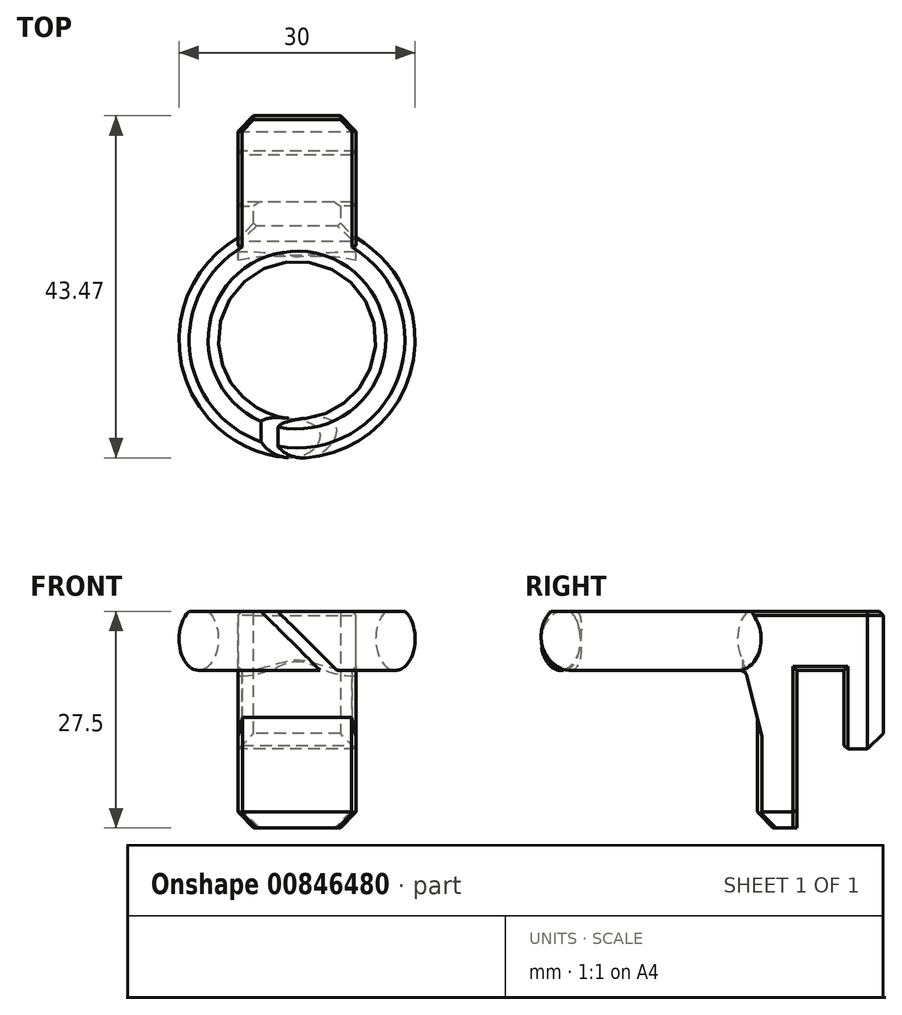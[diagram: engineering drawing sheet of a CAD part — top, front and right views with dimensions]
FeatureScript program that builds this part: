
annotation { "Feature Type Name" : "Feature", "Feature Type Description" : "" }
export const myFeature = defineFeature(function(context is Context, id is Id, definition is map)
    precondition{}
    {
        {
            var Q0;
            Q0=qCreatedBy(makeId("Front.planeOp"),FACE);
            var sketch = newSketch(context, id + "F0", { "sketchPlane" : qUnion([Q0])});
            skLineSegment(sketch, "E0", {"start": v(0, 10.58) * mm, "end": v(0, -9.7) * mm, "construction": true});
            skLineSegment(sketch, "E1", {"start": v(0, 0) * mm, "end": v(12.5, 0) * mm, "construction": true});
            skEllipse(sketch, "E2", {"center": v(12.5, 0) * mm, "majorRadius": 4 * mm, "minorRadius": 2.5 * mm, "majorAxis": v(0, 1)});
            skSolve(sketch);
        }
        {
            var Q0;
            Q0=qSketchRegion(id+"F0",true);
            var Q1;
            Q1=sQuery(id+"F0.wireOp",EDGE,"E0");
            revolve(context, id + "F1", {"surfaceOperationType" : NewSurfaceOperationType.NEW, "entities" : qUnion([Q0]), "axis" : qUnion([Q1]), "revolveType" : RevolveType.FULL});
        }
        {
            var Q0;
            Q0=qCreatedBy(makeId("Right.planeOp"),FACE);
            var sketch = newSketch(context, id + "F2", { "sketchPlane" : qUnion([Q0])});
            skLineSegment(sketch, "E3", {"start": v(12.5, 5) * mm, "end": v(28.5, 5) * mm});
            skLineSegment(sketch, "E4", {"start": v(28.5, 5) * mm, "end": v(28.5, -14) * mm});
            skLineSegment(sketch, "E5", {"start": v(28.5, -14) * mm, "end": v(23.5, -14) * mm});
            skLineSegment(sketch, "E6", {"start": v(23.5, -14) * mm, "end": v(23.5, -4) * mm});
            skLineSegment(sketch, "E7", {"start": v(23.5, -4) * mm, "end": v(17.5, -4) * mm});
            skLineSegment(sketch, "E8", {"start": v(17.5, -4) * mm, "end": v(17.5, -24) * mm});
            skLineSegment(sketch, "E9", {"start": v(17.5, -24) * mm, "end": v(12.5, -24) * mm});
            skLineSegment(sketch, "E10", {"start": v(12.5, -24) * mm, "end": v(12.5, 5) * mm});
            skSolve(sketch);
        }
        {
            var Q0;
            Q0=qSketchRegion(id+"F2",true);
            extrude(context, id + "F3", {"entities" : qUnion([Q0]), "operationType" : NewBodyOperationType.ADD, "endBound" : BoundingType.SYMMETRIC, "depth" : 15 * mm, "offsetDistance" : 25.4 * mm});
        }
        {
            var Q0;
            Q0=makeQuery(id+"F3.opExtrude","CAP_EDGE",EDGE,{"disambiguationData":[OSD([sQuery(id+"F2.wireOp",EDGE,"E3")])],"isStart":false});
            var Q1;
            Q1=makeQuery(id+"F3.opExtrude","CAP_EDGE",EDGE,{"disambiguationData":[OSD([sQuery(id+"F2.wireOp",EDGE,"E3")])],"isStart":true});
            var Q2;
            Q2=makeQuery(id+"F3.opExtrude","SWEPT_EDGE",EDGE,{"disambiguationData":[OSD([sQuery(id+"F2.wireOp",EDGE,"E3"),sQuery(id+"F2.wireOp",EDGE,"E4")])]});
            var Q3;
            Q3=makeQuery(id+"F3.opExtrude","CAP_EDGE",EDGE,{"disambiguationData":[OSD([sQuery(id+"F2.wireOp",EDGE,"E4")])],"isStart":true});
            var Q4;
            Q4=makeQuery(id+"F3.opExtrude","CAP_EDGE",EDGE,{"disambiguationData":[OSD([sQuery(id+"F2.wireOp",EDGE,"E4")])],"isStart":false});
            var Q5;
            Q5=makeQuery(id+"F3.opExtrude","SWEPT_EDGE",EDGE,{"disambiguationData":[OSD([sQuery(id+"F2.wireOp",EDGE,"E4"),sQuery(id+"F2.wireOp",EDGE,"E5")])]});
            var Q6;
            Q6=makeQuery(id+"F3.opExtrude","SWEPT_EDGE",EDGE,{"disambiguationData":[OSD([sQuery(id+"F2.wireOp",EDGE,"E9"),sQuery(id+"F2.wireOp",EDGE,"E10")])]});
            var Q7;
            Q7=makeQuery(id+"F3.opExtrude","CAP_EDGE",EDGE,{"disambiguationData":[OSD([sQuery(id+"F2.wireOp",EDGE,"E9")])],"isStart":false});
            var Q8;
            Q8=makeQuery(id+"F3.opExtrude","CAP_EDGE",EDGE,{"disambiguationData":[OSD([sQuery(id+"F2.wireOp",EDGE,"E9")])],"isStart":true});
            chamfer(context, id + "F4", {"entities" : qUnion([Q0, Q1, Q2, Q3, Q4, Q5, Q6, Q7, Q8]), "width" : 2 * mm, "tangentPropagation" : true});
        }
        {
            var Q0;
            Q0=makeQuery(id+"F3.opExtrude","CAP_EDGE",EDGE,{"disambiguationData":[OSD([sQuery(id+"F2.wireOp",EDGE,"E8")])],"isStart":true});
            var Q1;
            Q1=makeQuery(id+"F3.opExtrude","CAP_EDGE",EDGE,{"disambiguationData":[OSD([sQuery(id+"F2.wireOp",EDGE,"E8")])],"isStart":false});
            var Q2;
            Q2=makeQuery(id+"F3.opExtrude","CAP_EDGE",EDGE,{"disambiguationData":[OSD([sQuery(id+"F2.wireOp",EDGE,"E7")])],"isStart":false});
            var Q3;
            Q3=makeQuery(id+"F3.opExtrude","CAP_EDGE",EDGE,{"disambiguationData":[OSD([sQuery(id+"F2.wireOp",EDGE,"E7")])],"isStart":true});
            var Q4;
            Q4=makeQuery(id+"F3.opExtrude","CAP_EDGE",EDGE,{"disambiguationData":[OSD([sQuery(id+"F2.wireOp",EDGE,"E6")])],"isStart":true});
            var Q5;
            Q5=makeQuery(id+"F3.opExtrude","CAP_EDGE",EDGE,{"disambiguationData":[OSD([sQuery(id+"F2.wireOp",EDGE,"E6")])],"isStart":false});
            var Q6;
            Q6=makeQuery(id+"F3.opExtrude","SWEPT_EDGE",EDGE,{"disambiguationData":[OSD([sQuery(id+"F2.wireOp",EDGE,"E5"),sQuery(id+"F2.wireOp",EDGE,"E6")])]});
            var Q7;
            Q7=makeQuery(id+"F4.opChamfer","BLEND_EDGE",EDGE,{"blendedFrom":[makeQuery(id+"F3.opExtrude","CAP_EDGE",EDGE,{"disambiguationData":[OSD([sQuery(id+"F2.wireOp",EDGE,"E9")])],"isStart":false}),makeQuery(id+"F3.opExtrude","SWEPT_FACE",FACE,{"disambiguationData":[OSD([sQuery(id+"F2.wireOp",EDGE,"E8")])]})],"blendedInto":[makeQuery(id+"F3.opExtrude","SWEPT_FACE",FACE,{"disambiguationData":[OSD([sQuery(id+"F2.wireOp",EDGE,"E8")])]})]});
            var Q8;
            Q8=makeQuery(id+"F4.opChamfer","BLEND_EDGE",EDGE,{"blendedFrom":[makeQuery(id+"F3.opExtrude","CAP_EDGE",EDGE,{"disambiguationData":[OSD([sQuery(id+"F2.wireOp",EDGE,"E9")])],"isStart":true}),makeQuery(id+"F3.opExtrude","SWEPT_FACE",FACE,{"disambiguationData":[OSD([sQuery(id+"F2.wireOp",EDGE,"E8")])]})],"blendedInto":[makeQuery(id+"F3.opExtrude","SWEPT_FACE",FACE,{"disambiguationData":[OSD([sQuery(id+"F2.wireOp",EDGE,"E8")])]})]});
            chamfer(context, id + "F5", {"entities" : qUnion([Q0, Q1, Q2, Q3, Q4, Q5, Q6, Q7, Q8]), "width" : 0.5 * mm, "tangentPropagation" : true});
        }
        {
            var Q0;
            Q0=makeQuery(id+"F3.boolean.opBoolean","INTERSECT",EDGE,{"disambiguationData":[OD(0.0)],"derivedFrom":[makeQuery(id+"F1.opRevolve","SWEPT_FACE",FACE,{"disambiguationData":[OSD([sQuery(id+"F0.wireOp",EDGE,"E2")])]}),makeQuery(id+"F3.opExtrude","SWEPT_FACE",FACE,{"disambiguationData":[OSD([sQuery(id+"F2.wireOp",EDGE,"E10")])]})]});
            fillet(context, id + "F6", {"entities" : qUnion([Q0]), "radius" : 5 * mm, "tangentPropagation" : true, "allowEdgeOverflow" : false});
        }
        {
            var Q0;
            Q0=makeQuery(id+"F6.opFillet","BLEND_EDGE",EDGE,{"blendedFrom":[makeQuery(id+"F3.boolean.opBoolean","INTERSECT",EDGE,{"disambiguationData":[OD(0.0)],"derivedFrom":[makeQuery(id+"F1.opRevolve","SWEPT_FACE",FACE,{"disambiguationData":[OSD([sQuery(id+"F0.wireOp",EDGE,"E2")])]}),makeQuery(id+"F3.opExtrude","SWEPT_FACE",FACE,{"disambiguationData":[OSD([sQuery(id+"F2.wireOp",EDGE,"E10")])]})]}),makeQuery(id+"F3.opExtrude","SWEPT_FACE",FACE,{"disambiguationData":[OSD([sQuery(id+"F2.wireOp",EDGE,"E3")])]})],"blendedInto":[makeQuery(id+"F3.opExtrude","SWEPT_FACE",FACE,{"disambiguationData":[OSD([sQuery(id+"F2.wireOp",EDGE,"E3")])]})]});
            fillet(context, id + "F7", {"entities" : qUnion([Q0]), "radius" : 5 * mm, "tangentPropagation" : true, "allowEdgeOverflow" : false});
        }
        {
            var Q0;
            Q0=qCreatedBy(makeId("Right.planeOp"),FACE);
            var sketch = newSketch(context, id + "F8", { "sketchPlane" : qUnion([Q0])});
            skLineSegment(sketch, "E11", {"start": v(12.5, -10) * mm, "end": v(12.5, 0) * mm});
            skLineSegment(sketch, "E12", {"start": v(12.5, 0) * mm, "end": v(10, 0) * mm});
            skLineSegment(sketch, "E13", {"start": v(10, 0) * mm, "end": v(12.5, -10) * mm});
            skSolve(sketch);
        }
        {
            var Q0;
            Q0=qSketchRegion(id+"F8",true);
            extrude(context, id + "F9", {"entities" : qUnion([Q0]), "operationType" : NewBodyOperationType.ADD, "endBound" : BoundingType.SYMMETRIC, "depth" : 15 * mm, "offsetDistance" : 25.4 * mm});
        }
        {
            var Q0;
            Q0=makeQuery(id+"F9.boolean.opBoolean","INTERSECT",EDGE,{"derivedFrom":[makeQuery(id+"F1.opRevolve","SWEPT_FACE",FACE,{"disambiguationData":[OSD([sQuery(id+"F0.wireOp",EDGE,"E2")])]}),makeQuery(id+"F9.opExtrude","SWEPT_FACE",FACE,{"disambiguationData":[OSD([sQuery(id+"F8.wireOp",EDGE,"E13")])]})]});
            var Q1;
            Q1=makeQuery(id+"F9.opExtrude","SWEPT_EDGE",EDGE,{"disambiguationData":[OSD([sQuery(id+"F8.wireOp",EDGE,"E11"),sQuery(id+"F8.wireOp",EDGE,"E13")])]});
            fillet(context, id + "F10", {"entities" : qUnion([Q0, Q1]), "radius" : 1 * mm, "tangentPropagation" : true, "allowEdgeOverflow" : false});
        }
        {
            var Q0;
            {var subQ0=sQuery(id+"F2.wireOp",EDGE,"E9");Q0=makeQuery(id+"F4.opChamfer","BLEND_EDGE",EDGE,{"blendedFrom":[makeQuery(id+"F3.opExtrude","SWEPT_EDGE",EDGE,{"disambiguationData":[OSD([subQ0,sQuery(id+"F2.wireOp",EDGE,"E10")])]}),makeQuery(id+"F3.opExtrude","CAP_EDGE",EDGE,{"disambiguationData":[OSD([subQ0])],"isStart":true})],"blendedInto":[]});}
            var Q1;
            {var subQ0=sQuery(id+"F2.wireOp",EDGE,"E9");Q1=makeQuery(id+"F4.opChamfer","BLEND_EDGE",EDGE,{"blendedFrom":[makeQuery(id+"F3.opExtrude","SWEPT_EDGE",EDGE,{"disambiguationData":[OSD([subQ0,sQuery(id+"F2.wireOp",EDGE,"E10")])]}),makeQuery(id+"F3.opExtrude","CAP_EDGE",EDGE,{"disambiguationData":[OSD([subQ0])],"isStart":false})],"blendedInto":[]});}
            chamfer(context, id + "F11", {"entities" : qUnion([Q0, Q1]), "width" : 0.5 * mm, "tangentPropagation" : true});
        }
        {
            var Q0;
            {var subQ0=sQuery(id+"F2.wireOp",EDGE,"E10");var subQ1=sQuery(id+"F2.wireOp",EDGE,"E9");Q0=makeQuery(id+"F3.boolean.opBoolean","SPLIT",EDGE,{"disambiguationData":[TD([makeQuery(id+"F3.opExtrude","SWEPT_FACE",FACE,{"disambiguationData":[OSD([subQ1])]})])],"derivedFrom":makeQuery(id+"F3.opExtrude","CAP_EDGE",EDGE,{"disambiguationData":[OSD([subQ0])],"isStart":true})});}
            var Q1;
            {var subQ0=sQuery(id+"F2.wireOp",EDGE,"E10");var subQ1=sQuery(id+"F2.wireOp",EDGE,"E9");Q1=makeQuery(id+"F3.boolean.opBoolean","SPLIT",EDGE,{"disambiguationData":[TD([makeQuery(id+"F3.opExtrude","SWEPT_FACE",FACE,{"disambiguationData":[OSD([subQ1])]})])],"derivedFrom":makeQuery(id+"F3.opExtrude","CAP_EDGE",EDGE,{"disambiguationData":[OSD([subQ0])],"isStart":false})});}
            chamfer(context, id + "F12", {"entities" : qUnion([Q0, Q1]), "width" : 0.6 * mm, "tangentPropagation" : true});
        }
        {
            var Q0;
            Q0=qCreatedBy(makeId("Front.planeOp"),FACE);
            var sketch = newSketch(context, id + "F13", { "sketchPlane" : qUnion([Q0])});
            skLineSegment(sketch, "E14", {"start": v(-1.06, 0) * mm, "end": v(-6.06, 5) * mm});
            skLineSegment(sketch, "E15", {"start": v(-6.06, 5) * mm, "end": v(-3.94, 5) * mm});
            skLineSegment(sketch, "E16", {"start": v(-3.94, 5) * mm, "end": v(6.06, -5) * mm});
            skLineSegment(sketch, "E17", {"start": v(6.06, -5) * mm, "end": v(3.94, -5) * mm});
            skLineSegment(sketch, "E18", {"start": v(3.94, -5) * mm, "end": v(-1.06, 0) * mm});
            skSolve(sketch);
        }
        {
            var Q0;
            Q0=qSketchRegion(id+"F13",true);
            extrude(context, id + "F14", {"entities" : qUnion([Q0]), "operationType" : NewBodyOperationType.REMOVE, "depth" : 25 * mm, "offsetDistance" : 25 * mm});
        }
        {
            var Q0;
            Q0=qCreatedBy(makeId("Front.planeOp"),FACE);
            var sketch = newSketch(context, id + "F15", { "sketchPlane" : qUnion([Q0])});
            skLineSegment(sketch, "E19.bottom", {"start": v(-28.46, 11.77) * mm, "end": v(26.78, 11.77) * mm});
            skLineSegment(sketch, "E19.top", {"start": v(-28.46, 3.5) * mm, "end": v(26.78, 3.5) * mm});
            skLineSegment(sketch, "E19.left", {"start": v(-28.46, 11.77) * mm, "end": v(-28.46, 3.5) * mm});
            skLineSegment(sketch, "E19.right", {"start": v(26.78, 11.77) * mm, "end": v(26.78, 3.5) * mm});
            skSolve(sketch);
        }
        {
            var Q0;
            Q0=makeQuery(id+"F15.imprint","IMPRINT",FACE,{"disambiguationData":[TD([[makeQuery(id+"F15.imprint","IMPRINT",EDGE,{"derivedFrom":sQuery(id+"F15.wireOp",EDGE,"E19.bottom")}),-1.0]])]});
            extrude(context, id + "F16", {"entities" : qUnion([Q0]), "operationType" : NewBodyOperationType.REMOVE, "endBound" : BoundingType.SYMMETRIC, "oppositeDirection" : true, "depth" : 100 * mm, "offsetDistance" : 25 * mm});
        }
    });
